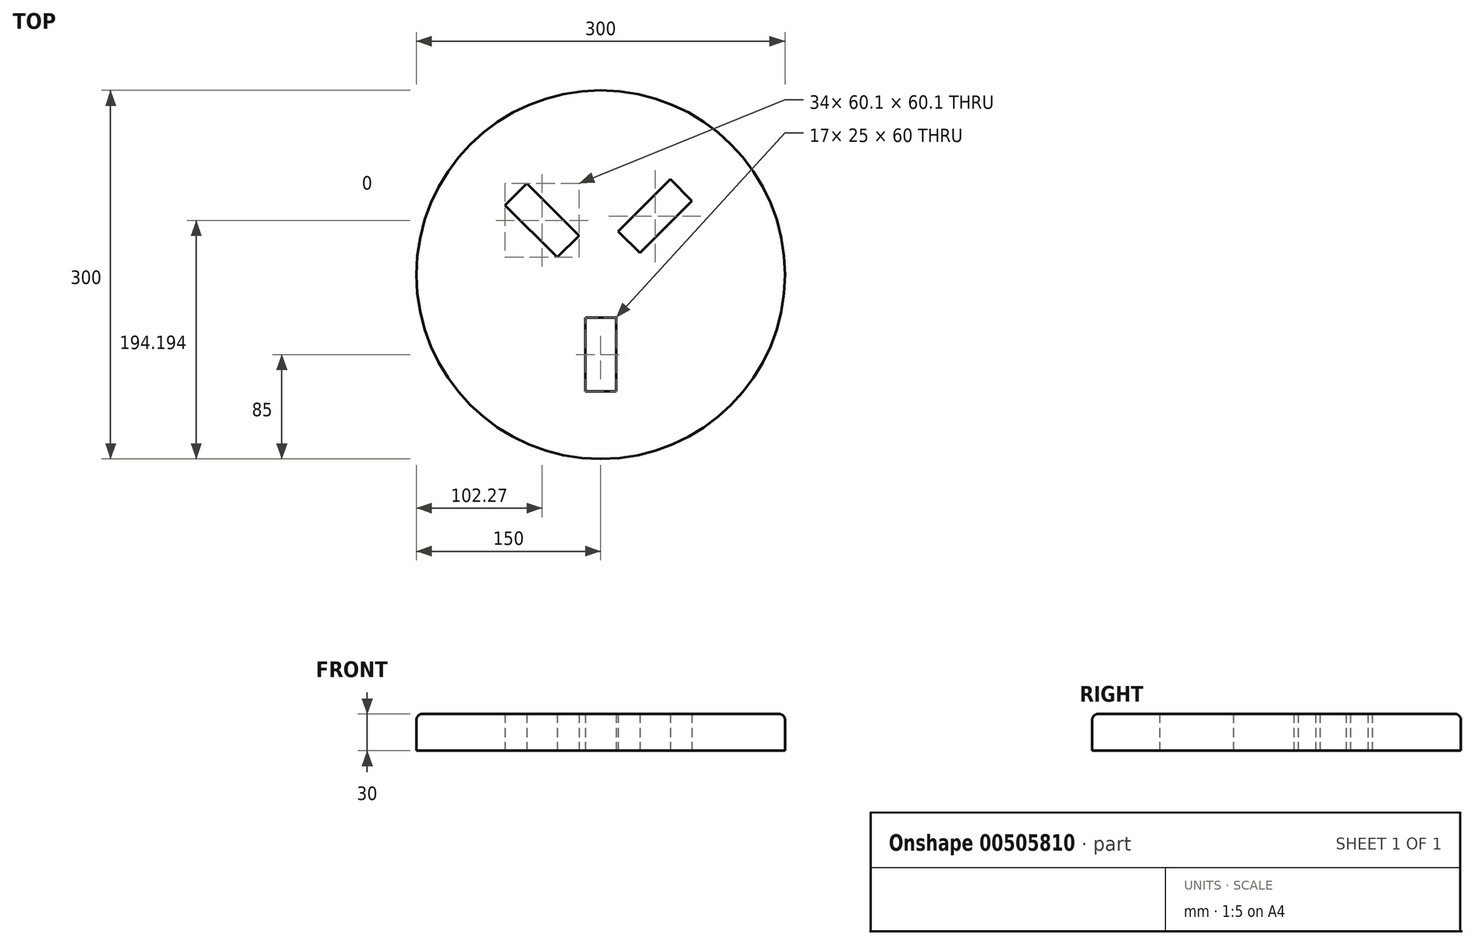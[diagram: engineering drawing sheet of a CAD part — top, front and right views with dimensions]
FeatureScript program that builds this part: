
annotation { "Feature Type Name" : "Feature", "Feature Type Description" : "" }
export const myFeature = defineFeature(function(context is Context, id is Id, definition is map)
    precondition{}
    {
        {
            var Q0;
            Q0=qCreatedBy(makeId("Top.planeOp"),FACE);
            var sketch = newSketch(context, id + "F0", { "sketchPlane" : qUnion([Q0])});
            skCircle(sketch, "E0", {"center": v(0, 0) * mm, "radius": 150 * mm});
            skLineSegment(sketch, "E1", {"start": v(-77.78, 56.57) * mm, "end": v(-60.1, 74.25) * mm});
            skLineSegment(sketch, "E2", {"start": v(74.25, 60.1) * mm, "end": v(56.57, 77.78) * mm});
            skLineSegment(sketch, "E3", {"start": v(-77.78, 56.57) * mm, "end": v(-35.36, 14.14) * mm});
            skLineSegment(sketch, "E4", {"start": v(-35.36, 14.14) * mm, "end": v(-17.68, 31.82) * mm});
            skLineSegment(sketch, "E5", {"start": v(-17.68, 31.82) * mm, "end": v(-60.1, 74.25) * mm});
            skLineSegment(sketch, "E6", {"start": v(56.57, 77.78) * mm, "end": v(14.14, 35.36) * mm});
            skLineSegment(sketch, "E7", {"start": v(14.14, 35.36) * mm, "end": v(31.82, 17.68) * mm});
            skLineSegment(sketch, "E8", {"start": v(74.25, 60.1) * mm, "end": v(31.82, 17.68) * mm});
            skLineSegment(sketch, "E9", {"start": v(0, -35) * mm, "end": v(-12.5, -35) * mm});
            skLineSegment(sketch, "E10", {"start": v(-12.5, -35) * mm, "end": v(-12.5, -95) * mm});
            skLineSegment(sketch, "E11", {"start": v(-12.5, -95) * mm, "end": v(12.5, -95) * mm});
            skLineSegment(sketch, "E12", {"start": v(12.5, -95) * mm, "end": v(12.5, -35) * mm});
            skLineSegment(sketch, "E13", {"start": v(12.5, -35) * mm, "end": v(0, -35) * mm});
            skSolve(sketch);
        }
        {
            var Q0;
            Q0=makeQuery(id+"F0.imprint","IMPRINT",FACE,{"disambiguationData":[TD([[makeQuery(id+"F0.imprint","IMPRINT",EDGE,{"derivedFrom":sQuery(id+"F0.wireOp",EDGE,"E0")}),1.0]])]});
            extrude(context, id + "F1", {"entities" : qUnion([Q0]), "depth" : 30 * mm, "offsetDistance" : 25 * mm});
        }
        {
            var Q0;
            Q0=makeQuery(id+"F1.opExtrude","CAP_EDGE",EDGE,{"disambiguationData":[OSD([sQuery(id+"F0.wireOp",EDGE,"E0")])],"isStart":false});
            fillet(context, id + "F2", {"entities" : qUnion([Q0]), "radius" : 5 * mm, "tangentPropagation" : true, "allowEdgeOverflow" : false});
        }
    });
